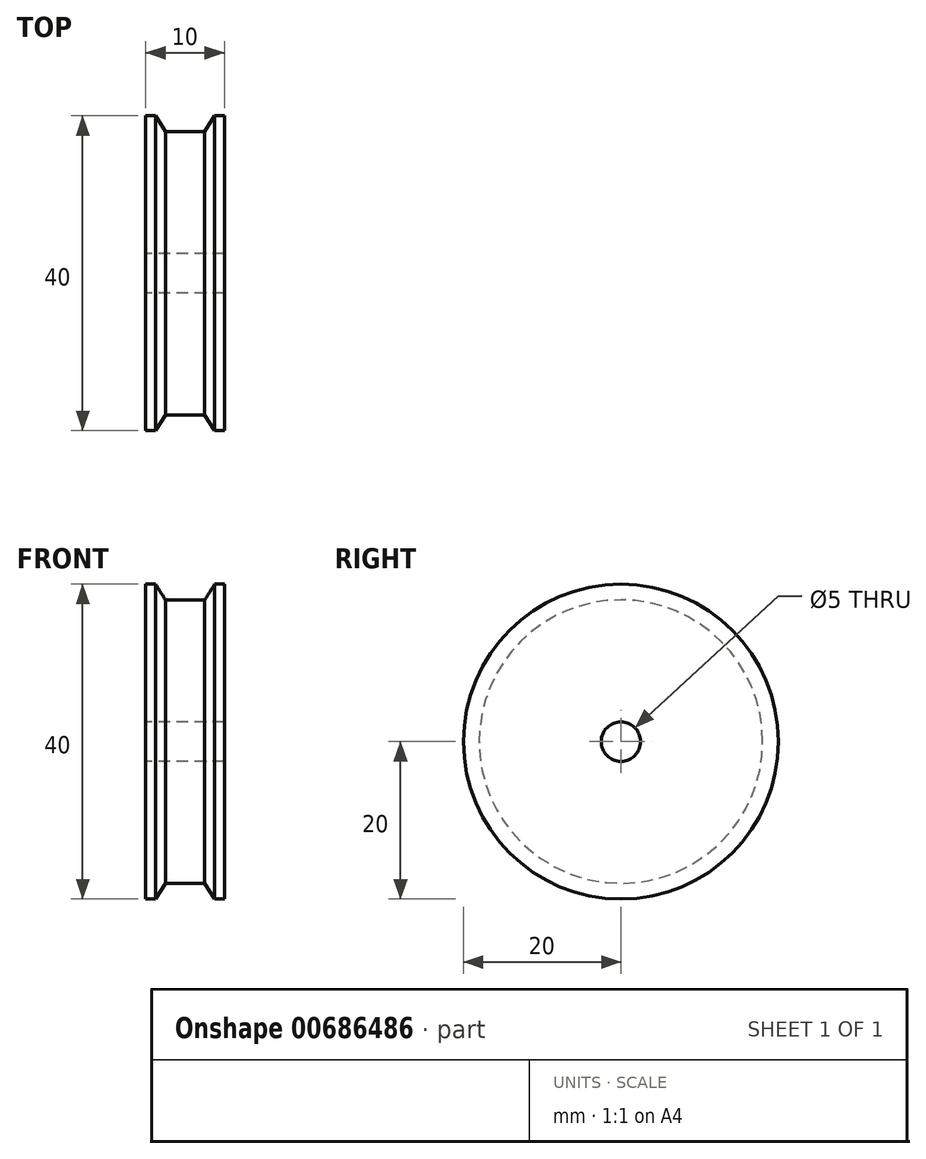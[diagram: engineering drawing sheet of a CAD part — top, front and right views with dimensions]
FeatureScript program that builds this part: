
annotation { "Feature Type Name" : "Feature", "Feature Type Description" : "" }
export const myFeature = defineFeature(function(context is Context, id is Id, definition is map)
    precondition{}
    {
        {
            var Q0;
            Q0=qCreatedBy(makeId("Front.planeOp"),FACE);
            var sketch = newSketch(context, id + "F0", { "sketchPlane" : qUnion([Q0])});
            skLineSegment(sketch, "E0.bottom", {"start": v(-5, 0) * mm, "end": v(5, 0) * mm});
            skLineSegment(sketch, "E0.top", {"start": v(-5, 5) * mm, "end": v(5, 5) * mm});
            skLineSegment(sketch, "E0.left", {"start": v(-5, 0) * mm, "end": v(-5, 5) * mm});
            skLineSegment(sketch, "E0.right", {"start": v(5, 0) * mm, "end": v(5, 5) * mm});
            skLineSegment(sketch, "E1.bottom", {"start": v(-2.5, 5) * mm, "end": v(2.5, 5) * mm});
            skLineSegment(sketch, "E1.top", {"start": v(-2.5, 12.5) * mm, "end": v(2.5, 12.5) * mm});
            skLineSegment(sketch, "E2.bottom", {"start": v(-5, 12.5) * mm, "end": v(5, 12.5) * mm});
            skLineSegment(sketch, "E2.left", {"start": v(-5, 12.5) * mm, "end": v(-5, 17.5) * mm});
            skLineSegment(sketch, "E2.right", {"start": v(5, 12.5) * mm, "end": v(5, 17.5) * mm});
            skLineSegment(sketch, "E3", {"start": v(-2.5, 15.5) * mm, "end": v(2.5, 15.5) * mm});
            skLineSegment(sketch, "E4", {"start": v(-11.34, -2.5) * mm, "end": v(11.97, -2.5) * mm});
            skLineSegment(sketch, "E5", {"start": v(-5, 12.5) * mm, "end": v(-5, 5) * mm});
            skLineSegment(sketch, "E6", {"start": v(5, 12.5) * mm, "end": v(5, 5) * mm});
            skLineSegment(sketch, "E7", {"start": v(-5, 17.5) * mm, "end": v(-3.75, 17.5) * mm});
            skLineSegment(sketch, "E8", {"start": v(-3.75, 17.5) * mm, "end": v(-2.5, 15.5) * mm});
            skLineSegment(sketch, "E9", {"start": v(5, 17.5) * mm, "end": v(3.75, 17.5) * mm});
            skLineSegment(sketch, "E10", {"start": v(3.75, 17.5) * mm, "end": v(2.5, 15.5) * mm});
            skSolve(sketch);
        }
        {
            var Q0;
            Q0 = qSketchRegion(id + "F0", true);
            var Q1;
            Q1=sQuery(id+"F0.wireOp",EDGE,"E4");
            revolve(context, id + "F1", {"entities" : qUnion([Q0]), "axis" : qUnion([Q1]), "revolveType" : RevolveType.FULL});
        }
    });
